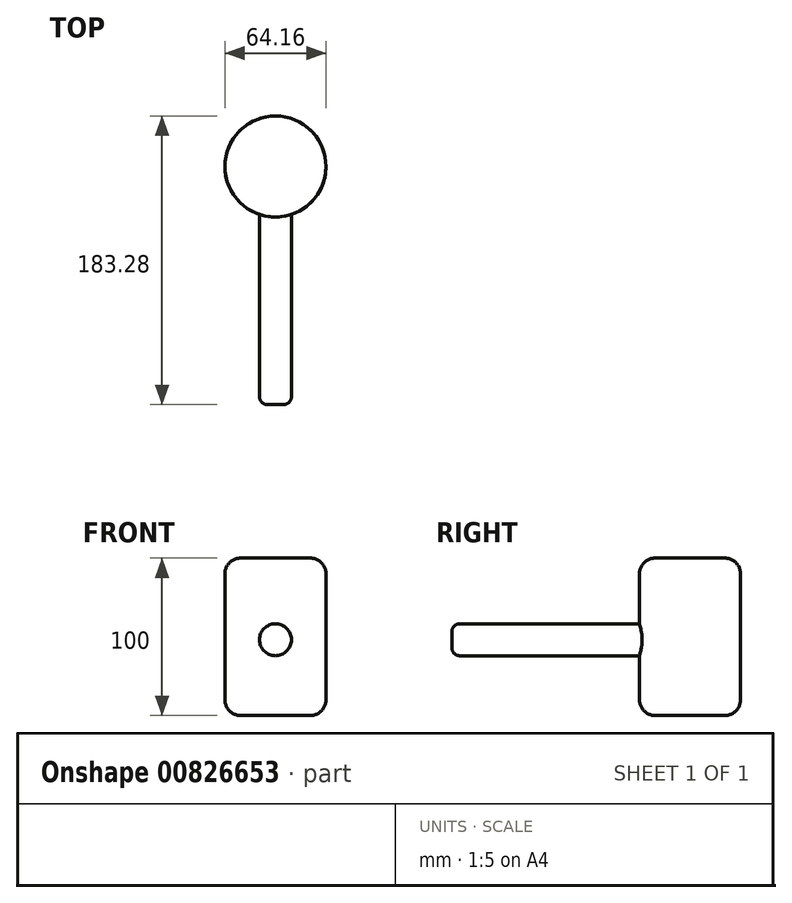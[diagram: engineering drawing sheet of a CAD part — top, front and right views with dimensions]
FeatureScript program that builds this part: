
annotation { "Feature Type Name" : "Feature", "Feature Type Description" : "" }
export const myFeature = defineFeature(function(context is Context, id is Id, definition is map)
    precondition{}
    {
        {
            var Q0;
            Q0=qCreatedBy(makeId("Top.planeOp"),FACE);
            var sketch = newSketch(context, id + "F0", { "sketchPlane" : qUnion([Q0])});
            skCircle(sketch, "E0", {"center": v(0, 0) * mm, "radius": 32.08 * mm});
            skSolve(sketch);
        }
        {
            var Q0;
            Q0=makeQuery(id+"F0.imprint","IMPRINT",FACE,{"disambiguationData":[TD([[makeQuery(id+"F0.imprint","IMPRINT",EDGE,{"derivedFrom":sQuery(id+"F0.wireOp",EDGE,"E0")}),1.0]])]});
            extrude(context, id + "F1", {"entities" : qUnion([Q0]), "depth" : 100 * mm, "offsetDistance" : 25 * mm});
        }
        {
            var Q0;
            Q0=makeQuery(id+"F1.opExtrude","CAP_EDGE",EDGE,{"disambiguationData":[OSD([sQuery(id+"F0.wireOp",EDGE,"E0")])],"isStart":false});
            var Q1;
            Q1=makeQuery(id+"F1.opExtrude","CAP_EDGE",EDGE,{"disambiguationData":[OSD([sQuery(id+"F0.wireOp",EDGE,"E0")])],"isStart":true});
            fillet(context, id + "F2", {"entities" : qUnion([Q0, Q1]), "radius" : 10 * mm, "tangentPropagation" : true, "allowEdgeOverflow" : false});
        }
        {
            var Q0;
            Q0=qCreatedBy(makeId("Front.planeOp"),FACE);
            cPlane(context, id + "F3", {"entities" : qUnion([Q0]), "cplaneType" : CPlaneType.OFFSET, "offset" : 26.2 * mm, "width" : 150 * mm, "height" : 150 * mm});
        }
        {
            var Q0;
            Q0=qCreatedBy(id+"F3.planeOp",FACE);
            var sketch = newSketch(context, id + "F4", { "sketchPlane" : qUnion([Q0])});
            skCircle(sketch, "E1", {"center": v(0, 48.12) * mm, "radius": 10.13 * mm});
            skSolve(sketch);
        }
        {
            var Q0;
            Q0 = qSketchRegion(id + "F4", true);
            extrude(context, id + "F5", {"entities" : qUnion([Q0]), "operationType" : NewBodyOperationType.ADD, "depth" : 125 * mm, "offsetDistance" : 25 * mm});
        }
        {
            var Q0;
            Q0=makeQuery(id+"F5.opExtrude","CAP_EDGE",EDGE,{"disambiguationData":[OSD([sQuery(id+"F4.wireOp",EDGE,"E1")])],"isStart":false});
            fillet(context, id + "F6", {"entities" : qUnion([Q0]), "radius" : 5 * mm, "tangentPropagation" : true, "allowEdgeOverflow" : false});
        }
    });
